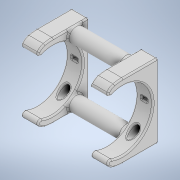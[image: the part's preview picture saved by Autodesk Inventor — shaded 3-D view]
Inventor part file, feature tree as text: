
AUTODESK INVENTOR PART (.ipt)
format: ipt  version: 2020 (Build 240168000, 168)  size: 774,656 bytes
history: native  units: mm
features: fillet x6, extrude x5, sketch x5, pattern_linear x1
ambient origin geometry x8: Origin, YZ Plane, XZ Plane, XY Plane, X Axis, Y Axis, Z Axis, Center Point
bodies: Solid1 (feature_tree)
feature tree (17):
  extrude  "Extrusion1"  Depth=2.5mm
  extrude  "Extrusion4"  Depth=26.0mm
  extrude  "Extrusion5"  Depth=0.85mm
  fillet  "Fillet2"  Radius=1.55mm
  fillet  "Fillet3"  Radius=1.8mm
  fillet  "Fillet4"  Radius=1.1mm
  fillet  "Fillet5"  Radius=21.0mm
  pattern_linear  "Rectangular Pattern1"  Spacing1=10.0mm  [1 undecoded]
  extrude  "Extrusion11"  Depth=10.5mm
  extrude  "Extrusion13"  Depth=3.5mm
  fillet  "Fillet8"  Radius=4.0mm
  fillet  "Fillet9"  Radius=10.0mm
  sketch  "Sketch1"  dims[d0=2.5mm d1=2.5mm]
  sketch  "Sketch6"  dims[d2=16.5mm d3=26.0mm]
  sketch  "Sketch7"  dims[d4=6.0mm d5=0.85mm d6=1.55mm d7=1.8mm d8=1.1mm d9=21.0mm d10=0.0mm]
  sketch  "Sketch16"  dims[d25=21.0mm]
  sketch  "Sketch19"  dims[d26=2.0mm d27=10.0mm d28=0.0mm d32=10.5mm d33=3.5mm d34=4.0mm d35=10.0mm d36=0.0mm d37=1.0mm d39=0.1mm d40=0.5mm d41=3.6mm d42=20.0mm d44=24.5mm d76=5.0mm d77=5.0mm d78=3.0mm d79=33.5mm d80=0.0mm d81=0.0mm d86=10.0mm d87=0.0mm d88=0.5mm d89=0.5mm d51=0.5mm d52=0.872665mm d53=0.5mm d54=0.872665mm]
note: 1 required parameter value undecoded (feature->parameter linkage not recoverable at this tier; creation-order binding heuristic only, values carry confidence <= 0.55)
